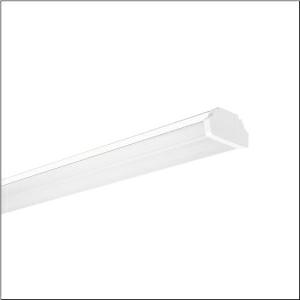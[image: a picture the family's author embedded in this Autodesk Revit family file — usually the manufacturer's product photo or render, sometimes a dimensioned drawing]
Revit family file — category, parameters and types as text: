
# Revit family: dus_31_gen_2_53bd812mv4cxd2_7e42
name_source: partatom
category: Lighting Fixtures
units: mm (PartAtom-declared; Revit-internal decimal feet)

## family parameters
Cut with Voids When Loaded = No
Host = Face
Light Source = No
Part Type = Normal
Room Calculation Point = No
Round Connector Dimension = Use Diameter
Shared = No

## types (1)
- --- (1 x LED, 12350 lm, 64.6 W, 4000K)
    Apparent Load = 65 VA
    CIE Flux Codes = 47 80 95 93 100
    Color Rendering = 80
    Color Temperature = 4000K
    Default Elevation = 1800 mm
    Description = DUS 31 Gen.2, luminaire insert, of sheet steel, coil coated, white, length: 1.535mm, width: 81mm, height: 90mm, 5x system unit, system units: 307mm, LED rated luminous flux: 12.350lm, light colour: 840, SDCM (Standard Deviation of Colour Matching)MacAdam ≤ 3 SDCM (initial), control gear: ON/OFF Multilumen, control gear: ECG, with plug, 3-pole, with phase selection, mains connection: 220..240V, AC, 50/60Hz, rated input power: 65W, through-wiring accessed according to module size, primary optical cover: cover, of PMMA, light emission: direct distribution, primary light characteristic: symmetric, protection rating (complete): IP20, protection rating (LED compartment): IP50, insulation class (complete): insulation class I (protective earthing), certification: CE, ENEC, VDE, UKCA, impact resistance: IK03, permissible ambient temperature for indoor applications: -35..+40°C, corresponds to IFS (International Featured Standards) requirements for safety and quality in the food industry, reducing of maximum allowable ambient temperature of 5°C with ceiling mounting, packaging unit: 1 piece
    Height = 95 mm
    Lamp = 1 x LED
    Lamp Light Flux = 12350 lm
    Lamp Power = 64.6 W
    Lamp count = 1
    Length = 1535 mm
    Luminous efficacy = 191 lm/W
    Manufacturer = Siteco
    ModVariant = No
    Model = 53BD812MV4CXD2
    Mounting Place = Ceiling
    Mounting Type = Pendant
    Number of Poles = 1
    OnlyDefault = Yes
    Power Factor = 1
    Product Name = DUS 31 Gen.2
    Product group = luminaire insert | ceiling pendant
    ProductGroupID = 901
    Protection Class = Protection class I
    Protection Degree = IP 20
    RLX_Detail_Level = 1
    RLX_Emergency_Light_Flux = 0 lm
    RLX_Emergency_Type = 0
    RLX_Emergency_Type_DB = No
    RlxData = <blob elided: 29937 chars, md5=95686a1f>
    Socket = socket
    Standby Power = 0 W
    System Light Flux = 12350 lm
    System Power = 65 W
    Type Comments = factory setting: luminous flux: 100 % | (A | C | E) | 152 mA
    Type Image = l_1319596.jpg
    URL = http://relux.com
    VarID = @adj_042397
    Voltage = 0 V
    Weight = 0.00 kg
    Width = 81 mm

## geometry (parser evidence)
native form markers: Blend x4, Sweep x13
no freeform markers — native parametric forms only
